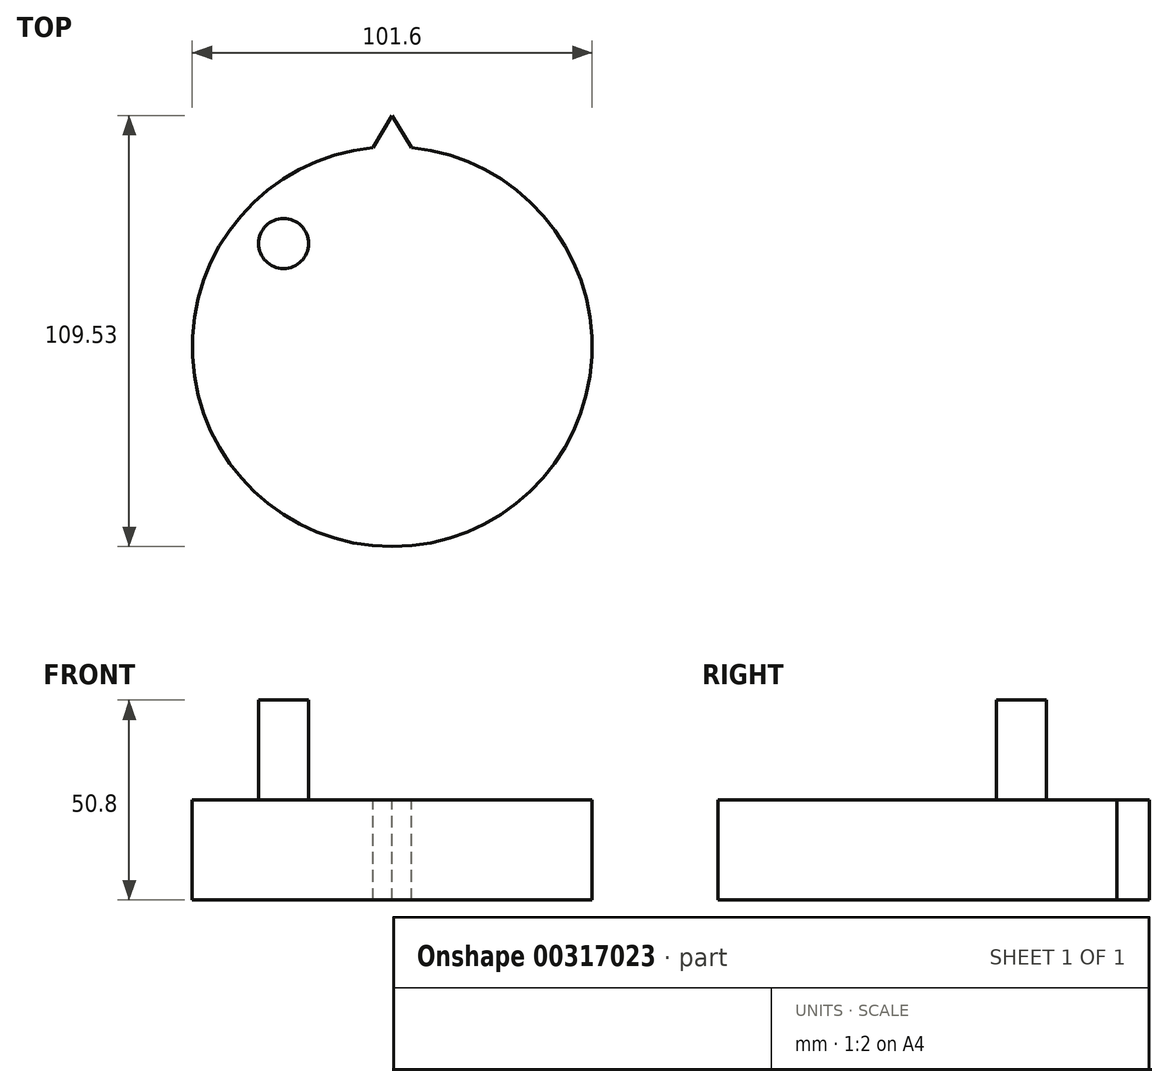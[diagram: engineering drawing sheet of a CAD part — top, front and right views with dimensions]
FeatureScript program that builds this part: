
annotation { "Feature Type Name" : "Feature", "Feature Type Description" : "" }
export const myFeature = defineFeature(function(context is Context, id is Id, definition is map)
    precondition{}
    {
        {
            var Q0;
            Q0=qCreatedBy(makeId("Top.planeOp"),FACE);
            var sketch = newSketch(context, id + "F0", { "sketchPlane" : qUnion([Q0])});
            skCircle(sketch, "E0", {"center": v(0, 0) * mm, "radius": 50.8 * mm});
            skSolve(sketch);
        }
        {
            var Q0;
            Q0 = qSketchRegion(id + "F0", true);
            extrude(context, id + "F1", {"entities" : qUnion([Q0]), "depth" : 25.4 * mm});
        }
        {
            var Q0;
            Q0=makeQuery(id+"F1.opExtrude","CAP_FACE",FACE,{"disambiguationData":[OSD([sQuery(id+"F0.wireOp",EDGE,"E0")])],"isStart":false});
            var sketch = newSketch(context, id + "F2", { "sketchPlane" : qUnion([Q0])});
            skCircle(sketch, "E1", {"center": v(-27.59, 26.21) * mm, "radius": 6.35 * mm});
            skSolve(sketch);
        }
        {
            var Q0;
            Q0 = qSketchRegion(id + "F2", true);
            extrude(context, id + "F3", {"entities" : qUnion([Q0]), "operationType" : NewBodyOperationType.ADD, "depth" : 25.4 * mm});
        }
        {
            var Q0;
            Q0=makeQuery(id+"F1.opExtrude","CAP_FACE",FACE,{"disambiguationData":[OSD([sQuery(id+"F0.wireOp",EDGE,"E0")])],"isStart":false});
            var sketch = newSketch(context, id + "F4", { "sketchPlane" : qUnion([Q0])});
            skLineSegment(sketch, "E2", {"start": v(0, 58.73) * mm, "end": v(-4.9, 50.56) * mm});
            skLineSegment(sketch, "E3", {"start": v(4.9, 50.56) * mm, "end": v(0, 58.73) * mm});
            skCircle(sketch, "E4.0", {"center": v(0, 0) * mm, "radius": 50.8 * mm});
            skLineSegment(sketch, "E5", {"start": v(-4.9, 50.56) * mm, "end": v(4.9, 50.56) * mm});
            skSolve(sketch);
        }
        {
            var Q0;
            Q0 = qSketchRegion(id + "F4", true);
            extrude(context, id + "F5", {"entities" : qUnion([Q0]), "operationType" : NewBodyOperationType.ADD, "oppositeDirection" : true, "depth" : 25.4 * mm});
        }
    });
